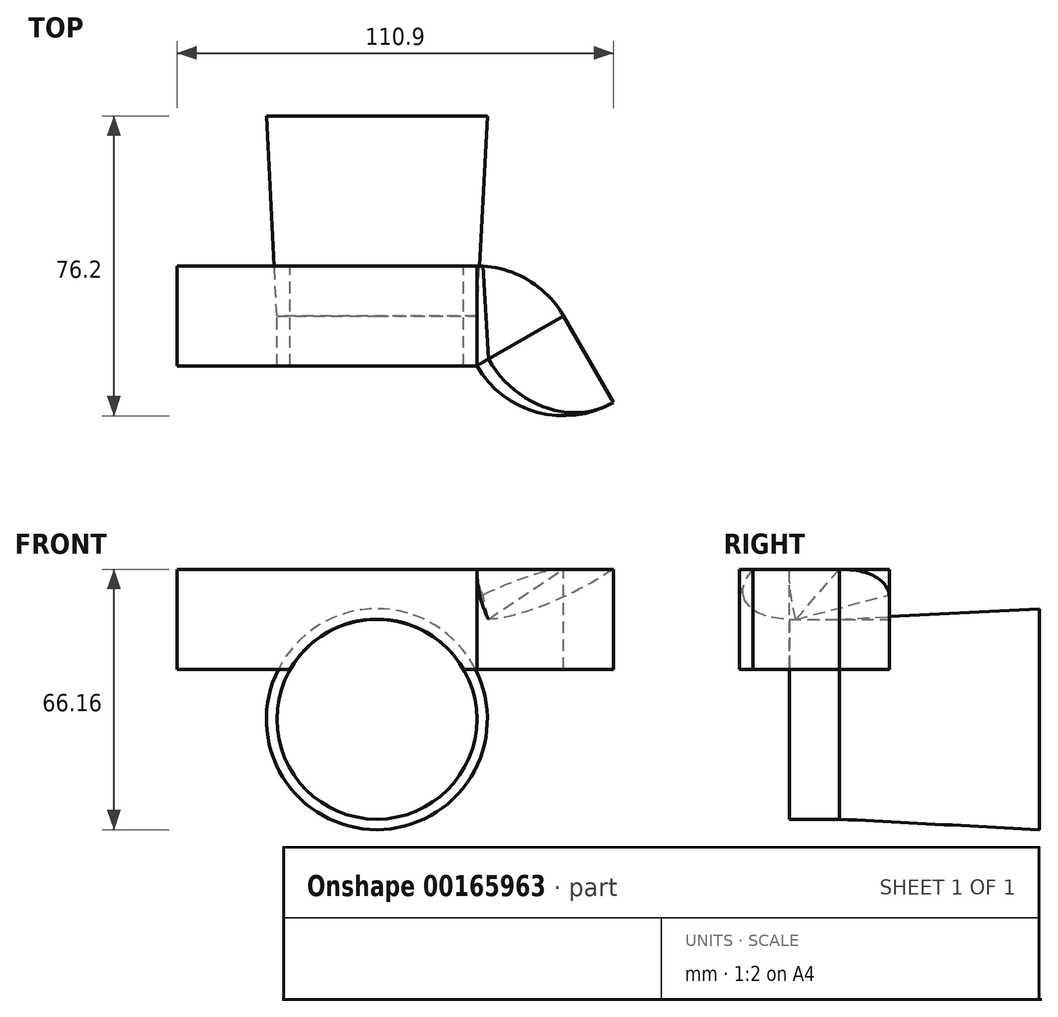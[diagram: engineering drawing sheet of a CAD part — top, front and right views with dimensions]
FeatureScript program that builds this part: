
annotation { "Feature Type Name" : "Feature", "Feature Type Description" : "" }
export const myFeature = defineFeature(function(context is Context, id is Id, definition is map)
    precondition{}
    {
        {
            var Q0;
            Q0=qCreatedBy(makeId("Front.planeOp"),FACE);
            var sketch = newSketch(context, id + "F0", { "sketchPlane" : qUnion([Q0])});
            skCircle(sketch, "E0", {"center": v(0, 0) * mm, "radius": 25.4 * mm});
            skLineSegment(sketch, "E1.bottom", {"start": v(25.4, 12.7) * mm, "end": v(-50.8, 12.7) * mm});
            skLineSegment(sketch, "E1.top", {"start": v(25.4, 38.1) * mm, "end": v(-50.8, 38.1) * mm});
            skLineSegment(sketch, "E1.left", {"start": v(25.4, 12.7) * mm, "end": v(25.4, 38.1) * mm});
            skLineSegment(sketch, "E1.right", {"start": v(-50.8, 12.7) * mm, "end": v(-50.8, 38.1) * mm});
            skSolve(sketch);
        }
        {
            var Q0;
            {var subQ1=sQuery(id+"F0.wireOp",EDGE,"E1.top");Q0=makeQuery(id+"F0.imprint","IMPRINT",FACE,{"disambiguationData":[TD([[makeQuery(id+"F0.imprint","IMPRINT",EDGE,{"derivedFrom":subQ1}),1.0]])]});}
            extrude(context, id + "F1", {"entities" : qUnion([Q0]), "endBound" : BoundingType.SYMMETRIC, "depth" : 25.4 * mm});
        }
        {
            var Q0;
            {var subQ0=sQuery(id+"F0.wireOp",EDGE,"E1.bottom");var subQ1=sQuery(id+"F0.wireOp",EDGE,"E0");var subQ2=makeQuery(id+"F0.imprint","INTERSECT",VERTEX,{"derivedFrom":[subQ1,subQ0]});Q0=makeQuery(id+"F0.imprint","IMPRINT",FACE,{"disambiguationData":[TD([[makeQuery(id+"F0.imprint","IMPRINT",EDGE,{"disambiguationData":[TD([[subQ2,-1.0]])],"derivedFrom":subQ1}),1.0]])]});}
            var Q1;
            Q1=makeQuery(id+"F1.opExtrude","CAP_FACE",FACE,{"disambiguationData":[OSD([sQuery(id+"F0.wireOp",EDGE,"E0"),sQuery(id+"F0.wireOp",EDGE,"E1.bottom"),sQuery(id+"F0.wireOp",EDGE,"E1.top"),sQuery(id+"F0.wireOp",EDGE,"E1.left"),sQuery(id+"F0.wireOp",EDGE,"E1.right")])],"isStart":false});
            extrude(context, id + "F2", {"entities" : qUnion([Q0]), "endBound" : BoundingType.UP_TO_SURFACE, "endBoundEntityFace" : qUnion([Q1]), "depth" : 50.8 * mm, "hasSecondDirection" : true, "secondDirectionOppositeDirection" : true, "secondDirectionDepth" : 50.8 * mm, "hasSecondDirectionDraft" : true, "secondDirectionDraftAngle" : 3 * degree});
        }
        {
            var Q0;
            Q0=makeQuery(id+"F1.opExtrude","SWEPT_FACE",FACE,{"disambiguationData":[OSD([sQuery(id+"F0.wireOp",EDGE,"E1.left")])]});
            var Q1;
            Q1=makeQuery(id+"F1.opExtrude","CAP_EDGE",EDGE,{"disambiguationData":[OSD([sQuery(id+"F0.wireOp",EDGE,"E1.left")])],"isStart":false});
            var Q2;
            Q2=makeQuery(id+"F1.opExtrude","CAP_EDGE",EDGE,{"disambiguationData":[OSD([sQuery(id+"F0.wireOp",EDGE,"E1.left")])],"isStart":false});
            revolve(context, id + "F3", {"entities" : qUnion([Q0]), "surfaceEntities" : qUnion([Q1]), "axis" : qUnion([Q2]), "revolveType" : RevolveType.ONE_DIRECTION, "oppositeDirection" : true, "angle" : 60 * degree});
        }
        {
            var Q0;
            Q0=makeQuery(id+"F3.opRevolve","CAP_FACE",FACE,{"disambiguationData":[OSD([sQuery(id+"F0.wireOp",EDGE,"E1.left")])],"isStart":false});
            var Q1;
            Q1=makeQuery(id+"F3.opRevolve","CAP_EDGE",EDGE,{"disambiguationData":[OSD([sQuery(id+"F0.wireOp",EDGE,"E1.left")])],"isStart":false});
            revolve(context, id + "F4", {"entities" : qUnion([Q0]), "axis" : qUnion([Q1]), "revolveType" : RevolveType.ONE_DIRECTION, "angle" : 90 * degree});
        }
        {
            var Q0;
            Q0=makeQuery(id+"F4.opRevolve","SWEPT_FACE",FACE,{"disambiguationData":[OSD([sQuery(id+"F0.wireOp",EDGE,"E1.top"),sQuery(id+"F0.wireOp",EDGE,"E1.left")])]});
            var Q1;
            Q1=makeQuery(id+"F3.opRevolve","SWEPT_FACE",FACE,{"disambiguationData":[OSD([sQuery(id+"F0.wireOp",EDGE,"E1.top"),sQuery(id+"F0.wireOp",EDGE,"E1.left")])]});
            var Q2;
            Q2=makeQuery(id+"F4.opRevolve","CAP_FACE",FACE,{"disambiguationData":[OSD([sQuery(id+"F0.wireOp",EDGE,"E1.left")])],"isStart":false});
            var Q3;
            Q3=makeQuery(id+"F4.opRevolve","CAP_EDGE",EDGE,{"disambiguationData":[OSD([sQuery(id+"F0.wireOp",EDGE,"E1.top"),sQuery(id+"F0.wireOp",EDGE,"E1.left")])],"isStart":false});
            var Q4;
            Q4=makeQuery(id+"F4.opRevolve","CAP_EDGE",EDGE,{"disambiguationData":[OSD([sQuery(id+"F0.wireOp",EDGE,"E1.top"),sQuery(id+"F0.wireOp",EDGE,"E1.left")])],"isStart":false});
            revolve(context, id + "F5", {"operationType" : NewBodyOperationType.REMOVE, "entities" : qUnion([Q0, Q1, Q2]), "surfaceEntities" : qUnion([Q3]), "axis" : qUnion([Q4]), "revolveType" : RevolveType.ONE_DIRECTION, "oppositeDirection" : true, "angle" : 30 * degree});
        }
    });
